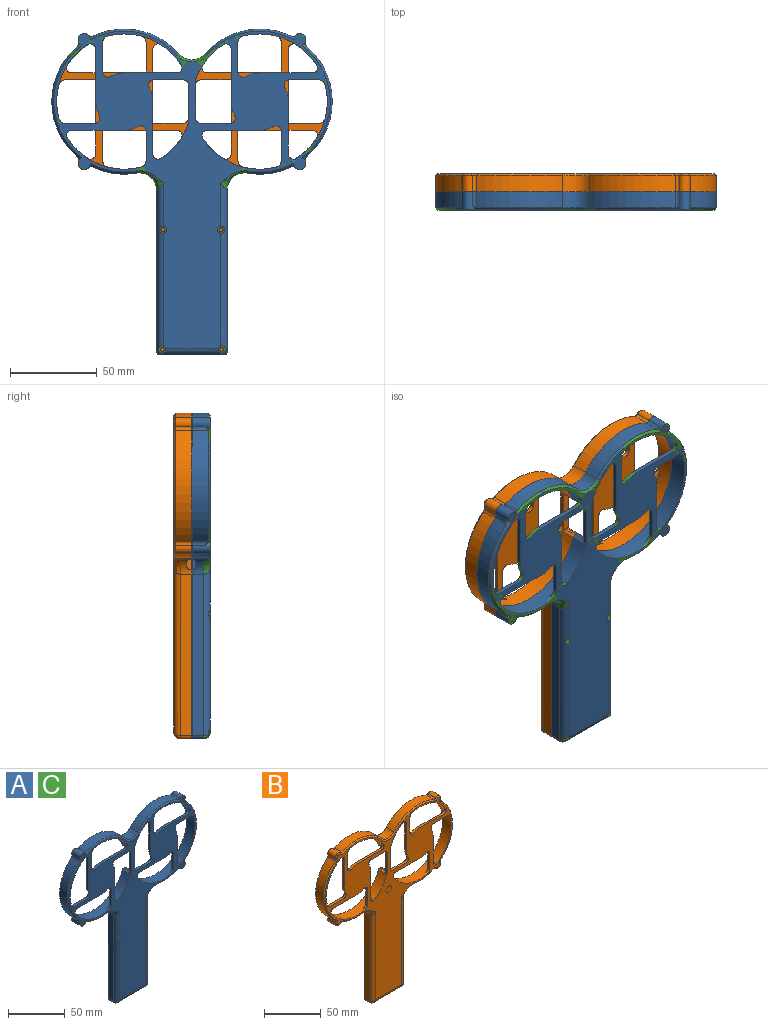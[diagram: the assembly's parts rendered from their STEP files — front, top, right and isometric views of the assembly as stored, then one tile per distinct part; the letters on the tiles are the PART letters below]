
ASSEMBLY  parts=3 mates=1
PART A: 186 faces, bbox 165x21x189.8 mm
  f0: plane 48.31x37.47mm, normal (0,1,0), area 1443.2mm2, adj f1,f2,f3,f5,f74,f105,f107,f110
  f1: cylinder r=41.8mm len=8.1mm, axis (0,-1,0), area 84.8mm2, adj f0,f4,f105,f185
  f2: plane 32.31x8.1mm, normal (1,0,0), area 230.3mm2, adj f0,f4,f71,f72,f76,f107,f166,f167
  f3: plane 32.31x8.1mm, normal (-1,0,0), area 190.4mm2, adj f0,f4,f110,f163,f164,f165,f185
  f4: plane 187.8x161.6mm, normal (0,1,0), area 2237.1mm2, adj f1,f2,f3,f13,f14,f15,f16,f17
  f5: plane 28.29x8.1mm, normal (0,0,1), area 199.2mm2, adj f0,f23,f107,f110,f155,f158,f159,f161
  f6: plane 28.29x8.1mm, normal (0,0,-1), area 199.2mm2, adj f23,f75,f108,f109,f155,f158,f160,f162
  f7: cylinder r=2.1mm len=4.2mm, axis (0,-1,0), area 31.7mm2, adj f125,f139
  f8: cylinder r=2.1mm len=4.2mm, axis (0,-1,0), area 31.7mm2, adj f126,f138
  f9: cylinder r=2.1mm len=4.2mm, axis (0,-1,0), area 31.7mm2, adj f129,f137
  f10: cylinder r=2.1mm len=4.2mm, axis (0,-1,0), area 31.7mm2, adj f124,f136
  f11: cylinder r=2.1mm len=4.2mm, axis (0,-1,0), area 31.7mm2, adj f127,f135
  f12: cylinder r=2.1mm len=4.2mm, axis (0,-1,0), area 31.7mm2, adj f128,f134
  f13: cylinder r=1.1mm len=7.8mm, axis (0,1,0), area 53.9mm2, adj f4,f116
  f14: cylinder r=1.1mm len=7.8mm, axis (0,1,0), area 53.9mm2, adj f4,f120
  f15: cylinder r=1.1mm len=7.8mm, axis (0,1,0), area 53.9mm2, adj f4,f129
  f16: cylinder r=1.1mm len=7.8mm, axis (0,1,0), area 53.9mm2, adj f4,f128
  f17: cylinder r=1.1mm len=7.8mm, axis (0,1,0), area 53.9mm2, adj f4,f127
  f18: cylinder r=1.1mm len=7.8mm, axis (0,1,0), area 53.9mm2, adj f4,f118
  f19: cylinder r=1.1mm len=7.8mm, axis (0,1,0), area 53.9mm2, adj f4,f122
  f20: cylinder r=1.1mm len=7.8mm, axis (0,1,0), area 53.9mm2, adj f4,f126
  f21: cylinder r=1.1mm len=7.8mm, axis (0,1,0), area 53.9mm2, adj f4,f125
  f22: cylinder r=1.1mm len=7.8mm, axis (0,1,0), area 53.9mm2, adj f4,f124
  f23: plane 24.29x2.8mm, normal (0,1,0), area 67.2mm2, adj f5,f6,f154,f157,f159,f160,f161,f162
  f24: plane 29x8.1mm, normal (0,0,1), area 234.9mm2, adj f4,f75,f111,f112
  f25: plane 63.48x8.1mm, normal (-1,0,0), area 514.2mm2, adj f4,f75,f109,f112
  f26: plane 63.48x8.1mm, normal (1,0,0), area 514.2mm2, adj f4,f75,f108,f111
  f27: cylinder r=41.8mm len=25.51mm, axis (0,1,0), area 241.6mm2, adj f4,f142,f143,f149,f178
  f28: plane 92.94x6.5mm, normal (-1,0,0), area 604.1mm2, adj f4,f115,f132,f142
  f29: plane 36.6x6.5mm, normal (0,0,-1), area 237.9mm2, adj f4,f114,f130,f132
  f30: plane 92.94x6.5mm, normal (1,0,0), area 552.8mm2, adj f4,f113,f130,f140,f163,f164,f165
  f31: cylinder r=41.8mm len=25.51mm, axis (0,1,0), area 241.6mm2, adj f4,f140,f141,f147,f182
  f32: cylinder r=3.5mm len=10.5mm, axis (0,1,0), area 109.8mm2, adj f4,f68,f147,f151,f181,f182
  f33: cylinder r=41.8mm len=63.95mm, axis (0,1,0), area 677.1mm2, adj f4,f151,f180,f181
  f34: cylinder r=3.5mm len=10.5mm, axis (0,1,0), area 109.8mm2, adj f4,f68,f146,f151,f180,f183
  f35: cylinder r=41.8mm len=49.73mm, axis (0,1,0), area 507.1mm2, adj f4,f106,f146,f183
  f36: cylinder r=41.8mm len=49.73mm, axis (0,1,0), area 507.1mm2, adj f4,f106,f144,f179
  f37: cylinder r=3.5mm len=10.5mm, axis (0,1,0), area 109.8mm2, adj f4,f68,f144,f152,f177,f179
  f38: cylinder r=41.8mm len=63.95mm, axis (0,1,0), area 677.1mm2, adj f4,f152,f176,f177
  f39: plane 16.92x2.4mm, normal (-1,0,0), area 40.6mm2, adj f68,f69,f94,f98
  f40: plane 30.26x2.4mm, normal (0,0,-1), area 72.6mm2, adj f59,f68,f69,f93
  f41: plane 30.26x2.4mm, normal (-1,0,0), area 72.6mm2, adj f42,f68,f69,f91
  f42: cylinder r=16.5mm len=8.04mm, axis (0,1,0), area 20.2mm2, adj f41,f68,f69,f92
  f43: plane 30.26x2.4mm, normal (0,0,1), area 72.6mm2, adj f44,f68,f69,f89
  f44: cylinder r=16.5mm len=8.04mm, axis (0,1,0), area 20.2mm2, adj f43,f68,f69,f90
  f45: cylinder r=39mm len=78mm, axis (0,1,0), area 2168.6mm2, adj f4,f62,f68,f69,f86,f89,f91,f93
  f46: plane 30.26x2.4mm, normal (1,0,0), area 72.6mm2, adj f47,f68,f69,f86
  f47: cylinder r=16.5mm len=8.04mm, axis (0,1,0), area 20.2mm2, adj f46,f68,f69,f87
  f48: plane 16.91x2.4mm, normal (0,0,-1), area 40.6mm2, adj f68,f69,f87,f88
  f49: plane 16.92x2.4mm, normal (-1,0,0), area 40.6mm2, adj f68,f69,f85,f95
  f50: cylinder r=39mm len=78mm, axis (0,1,0), area 2168.6mm2, adj f4,f64,f68,f69,f77,f79,f81,f84
  f51: plane 30.26x2.4mm, normal (0,0,-1), area 72.6mm2, adj f63,f68,f69,f84
  f52: plane 30.26x2.4mm, normal (-1,0,0), area 72.6mm2, adj f53,f68,f69,f81
  f53: cylinder r=16.5mm len=8.04mm, axis (0,1,0), area 20.2mm2, adj f52,f68,f69,f82
  f54: plane 16.91x2.4mm, normal (0,0,1), area 40.6mm2, adj f68,f69,f82,f83
  f55: plane 30.26x2.4mm, normal (0,0,1), area 72.6mm2, adj f56,f68,f69,f79
  f56: cylinder r=16.5mm len=8.04mm, axis (0,1,0), area 20.2mm2, adj f55,f68,f69,f80
  f57: plane 30.26x2.4mm, normal (1,0,0), area 72.6mm2, adj f58,f68,f69,f77
  f58: cylinder r=16.5mm len=8.04mm, axis (0,1,0), area 20.2mm2, adj f57,f68,f69,f78
  f59: cylinder r=16.5mm len=8.04mm, axis (0,1,0), area 20.2mm2, adj f40,f68,f69,f94
  f60: plane 16.92x2.4mm, normal (0,0,1), area 40.6mm2, adj f68,f69,f92,f100
  f61: plane 16.92x2.4mm, normal (1,0,0), area 40.6mm2, adj f68,f69,f90,f99
  f62: plane 22x2.4mm, normal (-1,0,0), area 52.8mm2, adj f45,f68,f69,f88
  f63: cylinder r=16.5mm len=8.04mm, axis (0,1,0), area 20.2mm2, adj f51,f68,f69,f85
  f64: plane 22x2.4mm, normal (1,0,0), area 52.8mm2, adj f50,f68,f69,f83
  f65: plane 16.92x2.4mm, normal (1,0,0), area 40.6mm2, adj f68,f69,f80,f97
  f66: plane 16.92x2.4mm, normal (0,0,-1), area 40.6mm2, adj f68,f69,f78,f96
  f67: cylinder r=3.5mm len=10.5mm, axis (0,1,0), area 109.8mm2, adj f4,f68,f149,f152,f176,f178
  f68: plane 183.14x159.74mm, normal (0,-1,0), area 7702.7mm2, adj f32,f34,f37,f39,f40,f41,f42,f43
  f69: plane 153.67x75.67mm, normal (0,1,0), area 2861.2mm2, adj f39,f40,f41,f42,f43,f44,f45,f46
  f70: plane 8.1x1.3mm, normal (0,0,-1), area 10.5mm2, adj f4,f69,f101,f102
  f71: plane 3.16x0.8mm, normal (0,0,1), area 2.5mm2, adj f2,f4,f142,f167
  f72: plane 7.81x0.8mm, normal (0,0,-1), area 6.2mm2, adj f2,f4,f142,f166
  f73: plane 8.1x1.3mm, normal (0,0,1), area 10.5mm2, adj f4,f69,f103,f104
  f74: cylinder r=41.8mm len=8.1mm, axis (0,-1,0), area 84.8mm2, adj f0,f4,f105,f184
  f75: plane 68x35mm, normal (0,1,0), area 2357.6mm2, adj f6,f24,f25,f26,f108,f109,f111,f112
  f76: plane 6.38x4mm, normal (0,1,0), area 18.7mm2, adj f2,f142,f166,f167
  f77: cylinder r=3mm len=4.63mm, axis (0,1,0), area 15.4mm2, adj f50,f57,f68,f69
  f78: cylinder r=3mm len=4.46mm, axis (0,1,0), area 15mm2, adj f58,f66,f68,f69
  f79: cylinder r=3mm len=4.63mm, axis (0,1,0), area 15.4mm2, adj f50,f55,f68,f69
  f80: cylinder r=3mm len=4.46mm, axis (0,1,0), area 15mm2, adj f56,f65,f68,f69
  f81: cylinder r=3mm len=4.63mm, axis (0,1,0), area 15.4mm2, adj f50,f52,f68,f69
  f82: cylinder r=3mm len=4.46mm, axis (0,1,0), area 15mm2, adj f53,f54,f68,f69
  f83: cylinder r=3mm len=3mm, axis (0,1,0), area 11.3mm2, adj f54,f64,f68,f69
  f84: cylinder r=3mm len=4.63mm, axis (0,1,0), area 15.4mm2, adj f50,f51,f68,f69
  f85: cylinder r=3mm len=4.46mm, axis (0,1,0), area 15mm2, adj f49,f63,f68,f69
  f86: cylinder r=3mm len=4.63mm, axis (0,1,0), area 15.4mm2, adj f45,f46,f68,f69
  f87: cylinder r=3mm len=4.46mm, axis (0,1,0), area 15mm2, adj f47,f48,f68,f69
  f88: cylinder r=3mm len=3mm, axis (0,-1,0), area 11.3mm2, adj f48,f62,f68,f69
  f89: cylinder r=3mm len=4.63mm, axis (0,1,0), area 15.4mm2, adj f43,f45,f68,f69
  f90: cylinder r=3mm len=4.46mm, axis (0,1,0), area 15mm2, adj f44,f61,f68,f69
  f91: cylinder r=3mm len=4.63mm, axis (0,1,0), area 15.4mm2, adj f41,f45,f68,f69
  f92: cylinder r=3mm len=4.46mm, axis (0,1,0), area 15mm2, adj f42,f60,f68,f69
  f93: cylinder r=3mm len=4.63mm, axis (0,1,0), area 15.4mm2, adj f40,f45,f68,f69
  f94: cylinder r=3mm len=4.46mm, axis (0,1,0), area 15mm2, adj f39,f59,f68,f69
  f95: cylinder r=4mm len=3.88mm, axis (0,1,0), area 12.7mm2, adj f49,f50,f68,f69
  f96: cylinder r=4mm len=3.88mm, axis (0,1,0), area 12.7mm2, adj f50,f66,f68,f69
  f97: cylinder r=4mm len=3.88mm, axis (0,1,0), area 12.7mm2, adj f50,f65,f68,f69
  f98: cylinder r=4mm len=3.88mm, axis (0,1,0), area 12.7mm2, adj f39,f45,f68,f69
  f99: cylinder r=4mm len=3.88mm, axis (0,1,0), area 12.7mm2, adj f45,f61,f68,f69
  f100: cylinder r=4mm len=3.88mm, axis (0,1,0), area 12.7mm2, adj f45,f60,f68,f69
  f101: cylinder r=2mm len=8.1mm, axis (0,1,0), area 19.6mm2, adj f4,f45,f69,f70
  f102: cylinder r=2mm len=8.1mm, axis (0,1,0), area 19.6mm2, adj f4,f50,f69,f70
  f103: cylinder r=2mm len=8.1mm, axis (0,1,0), area 19.6mm2, adj f4,f50,f69,f73
  f104: cylinder r=2mm len=8.1mm, axis (0,1,0), area 19.6mm2, adj f4,f45,f69,f73
  f105: cylinder r=10mm len=15.06mm, axis (0,1,0), area 138.1mm2, adj f0,f1,f4,f74
  f106: cylinder r=10mm len=15.06mm, axis (0,-1,0), area 158.6mm2, adj f4,f35,f36,f145
  f107: cylinder r=3mm len=8.1mm, axis (0,1,0), area 32.1mm2, adj f0,f2,f4,f5,f153
  f108: cylinder r=3mm len=8.1mm, axis (0,1,0), area 32.1mm2, adj f4,f6,f26,f75,f153
  f109: cylinder r=3mm len=8.1mm, axis (0,1,0), area 32.1mm2, adj f4,f6,f25,f75,f156
  f110: cylinder r=3mm len=8.1mm, axis (0,1,0), area 32.1mm2, adj f0,f3,f4,f5,f156
  f111: cylinder r=3mm len=8.1mm, axis (0,1,0), area 38.2mm2, adj f4,f24,f26,f75
  f112: cylinder r=3mm len=8.1mm, axis (0,1,0), area 38.2mm2, adj f4,f24,f25,f75
  f113: cylinder r=4mm len=97.44mm, axis (0,0,-1), area 551.9mm2, adj f0,f30,f68,f121,f123,f131,f141,f163
  f114: cylinder r=4mm len=36.6mm, axis (-1,0,0), area 209.4mm2, adj f29,f68,f117,f121,f131,f133
  f115: cylinder r=4mm len=97.44mm, axis (0,0,1), area 572.4mm2, adj f28,f68,f117,f119,f133,f143
  f116: plane 4.2x4.2mm, normal (0,-1,0), area 10.1mm2, adj f13,f117
  f117: cylinder r=2.1mm len=4.2mm, axis (0,-1,0), area 27mm2, adj f68,f114,f115,f116,f133
  f118: plane 4.2x4.2mm, normal (0,-1,0), area 10.1mm2, adj f18,f119
  f119: cylinder r=2.1mm len=4.2mm, axis (0,-1,0), area 32.2mm2, adj f68,f115,f118
  f120: plane 4.2x4.2mm, normal (0,-1,0), area 10.1mm2, adj f14,f121
  f121: cylinder r=2.1mm len=4.2mm, axis (0,-1,0), area 27mm2, adj f68,f113,f114,f120,f131
  f122: plane 4.2x4.2mm, normal (0,-1,0), area 10.1mm2, adj f19,f123
  f123: cylinder r=2.1mm len=4.2mm, axis (0,-1,0), area 32.2mm2, adj f68,f113,f122
  f124: plane 4.2x4.2mm, normal (0,-1,0), area 10.1mm2, adj f10,f22
  f125: plane 4.2x4.2mm, normal (0,-1,0), area 10.1mm2, adj f7,f21
  f126: plane 4.2x4.2mm, normal (0,-1,0), area 10.1mm2, adj f8,f20
  f127: plane 4.2x4.2mm, normal (0,-1,0), area 10.1mm2, adj f11,f17
  f128: plane 4.2x4.2mm, normal (0,-1,0), area 10.1mm2, adj f12,f16
  f129: plane 4.2x4.2mm, normal (0,-1,0), area 10.1mm2, adj f9,f15
  f130: cylinder r=2mm len=6.5mm, axis (0,-1,0), area 20.4mm2, adj f4,f29,f30,f131
  f131: bspline ~4.15x2.63mm, area 9.6mm2, adj f113,f114,f121,f130
  f132: cylinder r=2mm len=6.5mm, axis (0,1,0), area 20.4mm2, adj f4,f28,f29,f133
  f133: bspline ~4.15x2.63mm, area 9.6mm2, adj f114,f115,f117,f132
  f134: plane 4.2x4.2mm, normal (0,1,0), area 13.9mm2, adj f12
  f135: plane 4.2x4.2mm, normal (0,1,0), area 13.9mm2, adj f11
  f136: plane 4.2x4.2mm, normal (0,1,0), area 13.9mm2, adj f10
  f137: plane 4.2x4.2mm, normal (0,1,0), area 13.9mm2, adj f9
  f138: plane 4.2x4.2mm, normal (0,1,0), area 13.9mm2, adj f8
  f139: plane 4.2x4.2mm, normal (0,1,0), area 13.9mm2, adj f7
  f140: cylinder r=10mm len=11.68mm, axis (0,1,0), area 113.1mm2, adj f4,f30,f31,f141
  f141: bspline ~15.99x15.59mm, area 67.2mm2, adj f31,f113,f140,f148
  f142: cylinder r=10mm len=11.68mm, axis (0,1,0), area 100.5mm2, adj f4,f27,f28,f71,f72,f76,f143,f166
  f143: bspline ~15.99x15.59mm, area 67.2mm2, adj f27,f115,f142,f150
  f144: cone r=40.6mm half-angle=45deg, axis (0,1,0), area 96.2mm2, adj f36,f37,f68,f145,f179
  f145: cone r=11.2mm half-angle=45deg, axis (0,-1,0), area 30.7mm2, adj f68,f106,f144,f146
  f146: cone r=40.6mm half-angle=45deg, axis (0,1,0), area 96.2mm2, adj f34,f35,f68,f145,f183
  f147: cone r=40.6mm half-angle=45deg, axis (0,1,0), area 48.8mm2, adj f31,f32,f68,f148,f182
  f148: bspline ~15.66x6.83mm, area 12.3mm2, adj f68,f141,f147
  f149: cone r=40.6mm half-angle=45deg, axis (0,1,0), area 48.8mm2, adj f27,f67,f68,f150,f178
  f150: bspline ~15.66x6.83mm, area 12.3mm2, adj f68,f143,f149
  f151: cone r=40.6mm half-angle=45deg, axis (0,1,0), area 131.8mm2, adj f32,f33,f34,f68,f180,f181
  f152: cone r=40.6mm half-angle=45deg, axis (0,1,0), area 131.8mm2, adj f37,f38,f67,f68,f176,f177
  f153: plane 5x2.8mm, normal (1,0,0), area 14mm2, adj f4,f107,f108,f155
  f154: plane 5x0.8mm, normal (-1,0,0), area 4mm2, adj f23,f155,f159,f160
  f155: plane 3x2.8mm, normal (0,1,0), area 6mm2, adj f5,f6,f153,f154,f159,f160
  f156: plane 5x2.8mm, normal (-1,0,0), area 14mm2, adj f4,f109,f110,f158
  f157: plane 5x0.8mm, normal (1,0,0), area 4mm2, adj f23,f158,f161,f162
  f158: plane 3x2.8mm, normal (0,1,0), area 6mm2, adj f5,f6,f156,f157,f161,f162
  f159: cylinder r=1mm len=5mm, axis (0,-1,0), area 7.9mm2, adj f5,f23,f154,f155
  f160: cylinder r=1mm len=5mm, axis (0,-1,0), area 7.9mm2, adj f6,f23,f154,f155
  f161: cylinder r=1mm len=5mm, axis (0,1,0), area 7.9mm2, adj f5,f23,f157,f158
  f162: cylinder r=1mm len=5mm, axis (0,1,0), area 7.9mm2, adj f6,f23,f157,f158
  f163: plane 5.7x2.8mm, normal (0,0,-1), area 15.8mm2, adj f0,f3,f30,f113,f164
  f164: plane 12.5x2.8mm, normal (0,-1,0), area 35mm2, adj f3,f30,f163,f165
  f165: plane 5.7x2.8mm, normal (0,0,1), area 15.8mm2, adj f0,f3,f30,f113,f164
  f166: cylinder r=1mm len=7.81mm, axis (1,0,0), area 11.1mm2, adj f2,f72,f76,f142
  f167: cylinder r=1mm len=3.5mm, axis (-1,0,0), area 5.2mm2, adj f2,f71,f76,f142
  f168: plane 5.2x1.5mm, normal (0,0,1), area 7.8mm2, adj f0,f171,f172,f175
  f169: plane 6x1.5mm, normal (1,0,0), area 9mm2, adj f0,f171,f172,f173
  f170: plane 5.2x1.5mm, normal (0,0,-1), area 7.8mm2, adj f0,f171,f173,f174
  f171: plane 14x9.2mm, normal (0,1,0), area 92mm2, adj f2,f168,f169,f170,f172,f173,f174,f175
  f172: cylinder r=2mm len=2mm, axis (0,1,0), area 4.7mm2, adj f0,f168,f169,f171
  f173: cylinder r=2mm len=2mm, axis (0,-1,0), area 4.7mm2, adj f0,f169,f170,f171
  f174: cylinder r=2mm len=2mm, axis (0,1,0), area 4.7mm2, adj f0,f2,f170,f171
  f175: cylinder r=2mm len=2mm, axis (0,-1,0), area 4.7mm2, adj f0,f2,f168,f171
  f176: cylinder r=2mm len=9.3mm, axis (0,-1,0), area 21.8mm2, adj f4,f38,f67,f152
  f177: cylinder r=2mm len=9.3mm, axis (0,-1,0), area 21.8mm2, adj f4,f37,f38,f152
  f178: cylinder r=2mm len=9.3mm, axis (0,-1,0), area 21.8mm2, adj f4,f27,f67,f149
  f179: cylinder r=2mm len=9.3mm, axis (0,-1,0), area 21.8mm2, adj f4,f36,f37,f144
  f180: cylinder r=2mm len=9.3mm, axis (0,-1,0), area 21.8mm2, adj f4,f33,f34,f151
  f181: cylinder r=2mm len=9.3mm, axis (0,-1,0), area 21.8mm2, adj f4,f32,f33,f151
  f182: cylinder r=2mm len=9.3mm, axis (0,-1,0), area 21.8mm2, adj f4,f31,f32,f147
  f183: cylinder r=2mm len=9.3mm, axis (0,-1,0), area 21.8mm2, adj f4,f34,f35,f146
  f184: cylinder r=5mm len=8.1mm, axis (0,-1,0), area 39.2mm2, adj f0,f2,f4,f74
  f185: cylinder r=5mm len=8.1mm, axis (0,-1,0), area 39.2mm2, adj f0,f1,f3,f4
PART B: 181 faces, bbox 162.1x21x188.3 mm
  f0: plane 43.01x35mm, normal (0,1,0), area 1044.3mm2, adj f1,f2,f4,f5,f56,f92,f94,f128
  f1: cylinder r=41.8mm len=8.1mm, axis (0,-1,0), area 57.5mm2, adj f0,f57,f145,f159
  f2: plane 31.8x8.1mm, normal (1,0,0), area 181.9mm2, adj f0,f57,f94,f131,f146,f149,f158
  f3: plane 27x8.1mm, normal (0,0,1), area 218.7mm2, adj f57,f58,f90,f93
  f4: plane 27.18x8.1mm, normal (0,0,1), area 220.2mm2, adj f0,f57,f92,f94
  f5: plane 31.8x8.1mm, normal (-1,0,0), area 240.7mm2, adj f0,f53,f54,f57,f59,f92,f126,f127
  f6: plane 27.18x8.1mm, normal (0,0,-1), area 220.2mm2, adj f57,f58,f89,f91
  f7: plane 61.97x8.1mm, normal (1,0,0), area 502mm2, adj f57,f58,f91,f93
  f8: plane 61.97x8.1mm, normal (-1,0,0), area 502mm2, adj f57,f58,f89,f90
  f9: cylinder r=41.8mm len=25.51mm, axis (0,1,0), area 241.6mm2, adj f57,f124,f125,f157,f179
  f10: plane 92.94x6.5mm, normal (-1,0,0), area 604.1mm2, adj f57,f117,f120,f124
  f11: plane 36.6x6.5mm, normal (0,0,-1), area 237.9mm2, adj f57,f116,f118,f120
  f12: plane 92.94x6.5mm, normal (1,0,0), area 604.1mm2, adj f57,f115,f118,f122
  f13: cylinder r=41.8mm len=25.51mm, axis (0,1,0), area 241.6mm2, adj f57,f122,f123,f156,f161
  f14: cylinder r=3.5mm len=9.3mm, axis (0,1,0), area 90.8mm2, adj f57,f155,f156,f163
  f15: cylinder r=41.8mm len=63.95mm, axis (0,1,0), area 677.1mm2, adj f57,f154,f155,f165
  f16: cylinder r=3.5mm len=9.3mm, axis (0,1,0), area 90.8mm2, adj f57,f152,f154,f167
  f17: cylinder r=41.8mm len=49.73mm, axis (0,1,0), area 507.1mm2, adj f57,f88,f152,f169
  f18: cylinder r=41.8mm len=49.73mm, axis (0,1,0), area 507.1mm2, adj f57,f88,f153,f171
  f19: cylinder r=3.5mm len=9.3mm, axis (0,1,0), area 90.8mm2, adj f57,f150,f153,f173
  f20: cylinder r=41.8mm len=63.95mm, axis (0,1,0), area 677.1mm2, adj f57,f150,f151,f175
  f21: plane 16.92x2.4mm, normal (-1,0,0), area 40.6mm2, adj f50,f51,f77,f81
  f22: plane 30.26x2.4mm, normal (0,0,-1), area 72.6mm2, adj f41,f50,f51,f76
  f23: plane 30.26x2.4mm, normal (-1,0,0), area 72.6mm2, adj f24,f50,f51,f74
  f24: cylinder r=16.5mm len=8.04mm, axis (0,1,0), area 20.2mm2, adj f23,f50,f51,f75
  f25: plane 30.26x2.4mm, normal (0,0,1), area 72.6mm2, adj f26,f50,f51,f72
  f26: cylinder r=16.5mm len=8.04mm, axis (0,1,0), area 20.2mm2, adj f25,f50,f51,f73
  f27: cylinder r=39mm len=78mm, axis (0,1,0), area 2168.6mm2, adj f44,f50,f51,f57,f69,f72,f74,f76
  f28: plane 30.26x2.4mm, normal (1,0,0), area 72.6mm2, adj f29,f50,f51,f69
  f29: cylinder r=16.5mm len=8.04mm, axis (0,1,0), area 20.2mm2, adj f28,f50,f51,f70
  f30: plane 16.91x2.4mm, normal (0,0,-1), area 40.6mm2, adj f50,f51,f70,f71
  f31: plane 16.92x2.4mm, normal (-1,0,0), area 40.6mm2, adj f50,f51,f68,f78
  f32: cylinder r=39mm len=78mm, axis (0,1,0), area 2168.6mm2, adj f46,f50,f51,f57,f60,f62,f64,f67
  f33: plane 30.26x2.4mm, normal (0,0,-1), area 72.6mm2, adj f45,f50,f51,f67
  f34: plane 30.26x2.4mm, normal (-1,0,0), area 72.6mm2, adj f35,f50,f51,f64
  f35: cylinder r=16.5mm len=8.04mm, axis (0,1,0), area 20.2mm2, adj f34,f50,f51,f65
  f36: plane 16.91x2.4mm, normal (0,0,1), area 40.6mm2, adj f50,f51,f65,f66
  f37: plane 30.26x2.4mm, normal (0,0,1), area 72.6mm2, adj f38,f50,f51,f62
  f38: cylinder r=16.5mm len=8.04mm, axis (0,1,0), area 20.2mm2, adj f37,f50,f51,f63
  f39: plane 30.26x2.4mm, normal (1,0,0), area 72.6mm2, adj f40,f50,f51,f60
  f40: cylinder r=16.5mm len=8.04mm, axis (0,1,0), area 20.2mm2, adj f39,f50,f51,f61
  f41: cylinder r=16.5mm len=8.04mm, axis (0,1,0), area 20.2mm2, adj f22,f50,f51,f77
  f42: plane 16.92x2.4mm, normal (0,0,1), area 40.6mm2, adj f50,f51,f75,f83
  f43: plane 16.92x2.4mm, normal (1,0,0), area 40.6mm2, adj f50,f51,f73,f82
  f44: plane 22x2.4mm, normal (-1,0,0), area 52.8mm2, adj f27,f50,f51,f71
  f45: cylinder r=16.5mm len=8.04mm, axis (0,1,0), area 20.2mm2, adj f33,f50,f51,f68
  f46: plane 22x2.4mm, normal (1,0,0), area 52.8mm2, adj f32,f50,f51,f66
  f47: plane 16.92x2.4mm, normal (1,0,0), area 40.6mm2, adj f50,f51,f63,f80
  f48: plane 16.92x2.4mm, normal (0,0,-1), area 40.6mm2, adj f50,f51,f61,f79
  f49: cylinder r=3.5mm len=9.3mm, axis (0,1,0), area 90.8mm2, adj f57,f151,f157,f177
  f50: plane 183.14x159.74mm, normal (0,-1,0), area 7666.5mm2, adj f21,f22,f23,f24,f25,f26,f27,f28
  f51: plane 153.67x75.67mm, normal (0,1,0), area 2861.2mm2, adj f21,f22,f23,f24,f25,f26,f27,f28
  f52: plane 8.1x1.3mm, normal (0,0,-1), area 10.5mm2, adj f51,f57,f84,f85
  f53: plane 7.81x1.1mm, normal (0,0,-1), area 8.6mm2, adj f5,f57,f122,f126
  f54: plane 3.16x1.1mm, normal (0,0,1), area 3.5mm2, adj f5,f57,f122,f127
  f55: plane 8.1x1.3mm, normal (0,0,1), area 10.5mm2, adj f51,f57,f86,f87
  f56: cylinder r=41.8mm len=8.1mm, axis (0,-1,0), area 57.5mm2, adj f0,f57,f144,f158
  f57: plane 187.8x161.6mm, normal (0,1,0), area 2390.9mm2, adj f1,f2,f3,f4,f5,f6,f7,f8
  f58: plane 68x35mm, normal (0,1,0), area 2342.2mm2, adj f3,f6,f7,f8,f89,f90,f91,f93
  f59: plane 5.34x2mm, normal (0,1,0), area 9.2mm2, adj f5,f122,f126,f127
  f60: cylinder r=3mm len=4.63mm, axis (0,1,0), area 15.4mm2, adj f32,f39,f50,f51
  f61: cylinder r=3mm len=4.46mm, axis (0,1,0), area 15mm2, adj f40,f48,f50,f51
  f62: cylinder r=3mm len=4.63mm, axis (0,1,0), area 15.4mm2, adj f32,f37,f50,f51
  f63: cylinder r=3mm len=4.46mm, axis (0,1,0), area 15mm2, adj f38,f47,f50,f51
  f64: cylinder r=3mm len=4.63mm, axis (0,1,0), area 15.4mm2, adj f32,f34,f50,f51
  f65: cylinder r=3mm len=4.46mm, axis (0,1,0), area 15mm2, adj f35,f36,f50,f51
  f66: cylinder r=3mm len=3mm, axis (0,1,0), area 11.3mm2, adj f36,f46,f50,f51
  f67: cylinder r=3mm len=4.63mm, axis (0,1,0), area 15.4mm2, adj f32,f33,f50,f51
  f68: cylinder r=3mm len=4.46mm, axis (0,1,0), area 15mm2, adj f31,f45,f50,f51
  f69: cylinder r=3mm len=4.63mm, axis (0,1,0), area 15.4mm2, adj f27,f28,f50,f51
  f70: cylinder r=3mm len=4.46mm, axis (0,1,0), area 15mm2, adj f29,f30,f50,f51
  f71: cylinder r=3mm len=3mm, axis (0,-1,0), area 11.3mm2, adj f30,f44,f50,f51
  f72: cylinder r=3mm len=4.63mm, axis (0,1,0), area 15.4mm2, adj f25,f27,f50,f51
  f73: cylinder r=3mm len=4.46mm, axis (0,1,0), area 15mm2, adj f26,f43,f50,f51
  f74: cylinder r=3mm len=4.63mm, axis (0,1,0), area 15.4mm2, adj f23,f27,f50,f51
  f75: cylinder r=3mm len=4.46mm, axis (0,1,0), area 15mm2, adj f24,f42,f50,f51
  f76: cylinder r=3mm len=4.63mm, axis (0,1,0), area 15.4mm2, adj f22,f27,f50,f51
  f77: cylinder r=3mm len=4.46mm, axis (0,1,0), area 15mm2, adj f21,f41,f50,f51
  f78: cylinder r=4mm len=3.88mm, axis (0,1,0), area 12.7mm2, adj f31,f32,f50,f51
  f79: cylinder r=4mm len=3.88mm, axis (0,1,0), area 12.7mm2, adj f32,f48,f50,f51
  f80: cylinder r=4mm len=3.88mm, axis (0,1,0), area 12.7mm2, adj f32,f47,f50,f51
  f81: cylinder r=4mm len=3.88mm, axis (0,1,0), area 12.7mm2, adj f21,f27,f50,f51
  f82: cylinder r=4mm len=3.88mm, axis (0,1,0), area 12.7mm2, adj f27,f43,f50,f51
  f83: cylinder r=4mm len=3.88mm, axis (0,1,0), area 12.7mm2, adj f27,f42,f50,f51
  f84: cylinder r=2mm len=8.1mm, axis (0,1,0), area 19.6mm2, adj f27,f51,f52,f57
  f85: cylinder r=2mm len=8.1mm, axis (0,1,0), area 19.6mm2, adj f32,f51,f52,f57
  f86: cylinder r=2mm len=8.1mm, axis (0,1,0), area 19.6mm2, adj f32,f51,f55,f57
  f87: cylinder r=2mm len=8.1mm, axis (0,1,0), area 19.6mm2, adj f27,f51,f55,f57
  f88: cylinder r=10mm len=15.06mm, axis (0,-1,0), area 158.6mm2, adj f17,f18,f57,f170
  f89: cylinder r=3.5mm len=8.1mm, axis (0,1,0), area 38.6mm2, adj f6,f8,f57,f58
  f90: cylinder r=4mm len=8.1mm, axis (0,1,0), area 50.9mm2, adj f3,f8,f57,f58
  f91: cylinder r=3.5mm len=8.1mm, axis (0,1,0), area 38.6mm2, adj f6,f7,f57,f58
  f92: cylinder r=3.5mm len=8.1mm, axis (0,1,0), area 38.6mm2, adj f0,f4,f5,f57
  f93: cylinder r=4mm len=8.1mm, axis (0,1,0), area 50.9mm2, adj f3,f7,f57,f58
  f94: cylinder r=3.5mm len=8.1mm, axis (0,1,0), area 38.6mm2, adj f0,f2,f4,f57
  f95: cylinder r=1.5mm len=5mm, axis (0,1,0), area 47.1mm2, adj f57,f96
  f96: plane 3x3mm, normal (0,1,0), area 7.1mm2, adj f95
  f97: cylinder r=1.5mm len=5mm, axis (0,1,0), area 47.1mm2, adj f57,f98
  f98: plane 3x3mm, normal (0,1,0), area 7.1mm2, adj f97
  f99: cylinder r=1.5mm len=5mm, axis (0,1,0), area 47.1mm2, adj f57,f100
  f100: plane 3x3mm, normal (0,1,0), area 7.1mm2, adj f99
  f101: cylinder r=1.5mm len=5mm, axis (0,1,0), area 47.1mm2, adj f57,f102
  f102: plane 3x3mm, normal (0,1,0), area 7.1mm2, adj f101
  f103: cylinder r=1.5mm len=5mm, axis (0,1,0), area 47.1mm2, adj f57,f104
  f104: plane 3x3mm, normal (0,1,0), area 7.1mm2, adj f103
  f105: cylinder r=1.5mm len=5mm, axis (0,1,0), area 47.1mm2, adj f57,f106
  f106: plane 3x3mm, normal (0,1,0), area 7.1mm2, adj f105
  f107: cylinder r=1.5mm len=5mm, axis (0,1,0), area 47.1mm2, adj f57,f108
  f108: plane 3x3mm, normal (0,1,0), area 7.1mm2, adj f107
  f109: cylinder r=1.5mm len=5mm, axis (0,1,0), area 47.1mm2, adj f57,f110
  f110: plane 3x3mm, normal (0,1,0), area 7.1mm2, adj f109
  f111: cylinder r=1.5mm len=5mm, axis (0,1,0), area 47.1mm2, adj f57,f112
  f112: plane 3x3mm, normal (0,1,0), area 7.1mm2, adj f111
  f113: cylinder r=1.5mm len=5mm, axis (0,1,0), area 47.1mm2, adj f57,f114
  f114: plane 3x3mm, normal (0,1,0), area 7.1mm2, adj f113
  f115: cylinder r=4mm len=97.44mm, axis (0,0,-1), area 591.8mm2, adj f12,f50,f119,f123
  f116: cylinder r=4mm len=36.6mm, axis (-1,0,0), area 217.4mm2, adj f11,f50,f119,f121
  f117: cylinder r=4mm len=97.44mm, axis (0,0,1), area 591.8mm2, adj f10,f50,f121,f125
  f118: cylinder r=2mm len=6.5mm, axis (0,-1,0), area 20.4mm2, adj f11,f12,f57,f119
  f119: bspline ~4.78x4mm, area 8.7mm2, adj f115,f116,f118
  f120: cylinder r=2mm len=6.5mm, axis (0,1,0), area 20.4mm2, adj f10,f11,f57,f121
  f121: bspline ~4.78x4mm, area 8.7mm2, adj f116,f117,f120
  f122: cylinder r=10mm len=11.68mm, axis (0,1,0), area 91.4mm2, adj f12,f13,f53,f54,f57,f59,f123,f126
  f123: bspline ~15.99x15.59mm, area 67.2mm2, adj f13,f115,f122,f160
  f124: cylinder r=10mm len=11.68mm, axis (0,1,0), area 113.1mm2, adj f9,f10,f57,f125
  f125: bspline ~15.99x15.59mm, area 67.2mm2, adj f9,f117,f124,f180
  f126: cylinder r=2mm len=7.81mm, axis (1,0,0), area 20.7mm2, adj f5,f53,f59,f122
  f127: cylinder r=2mm len=3.95mm, axis (-1,0,0), area 11.2mm2, adj f5,f54,f59,f122
  f128: plane 13x3.6mm, normal (0,0,1), area 46.8mm2, adj f0,f131,f146,f147
  f129: plane 13x3.6mm, normal (1,0,0), area 46.8mm2, adj f0,f131,f147,f148
  f130: plane 13x3.6mm, normal (0,0,-1), area 46.8mm2, adj f0,f131,f148,f149
  f131: plane 21x17mm, normal (0,1,0), area 289mm2, adj f2,f128,f129,f130,f146,f147,f148,f149
  f132: plane 8.1x3.7mm, normal (1,0,0), area 30mm2, adj f0,f57,f142,f145
  f133: plane 8.9x8.1mm, normal (0,0,-1), area 72.1mm2, adj f0,f57,f142,f143
  f134: plane 8.1x3.7mm, normal (-1,0,0), area 30mm2, adj f0,f57,f143,f144
  f135: plane 8.9x8.1mm, normal (-1,0,0), area 72.1mm2, adj f57,f136,f138,f141
  f136: plane 8.9x8.1mm, normal (0,0,-1), area 72.1mm2, adj f57,f135,f137,f141
  f137: plane 8.9x8.1mm, normal (1,0,0), area 72.1mm2, adj f57,f136,f138,f141
  f138: plane 8.9x8.1mm, normal (0,0,1), area 72.1mm2, adj f57,f135,f137,f141
  f139: plane 7x7mm, normal (0,1,0), area 38.5mm2, adj f140
  f140: cylinder r=3.5mm len=7mm, axis (0,1,0), area 46.2mm2, adj f139,f141
  f141: plane 8.9x8.9mm, normal (0,1,0), area 40.7mm2, adj f135,f136,f137,f138,f140
  f142: cylinder r=2mm len=8.1mm, axis (0,1,0), area 25.4mm2, adj f0,f57,f132,f133
  f143: cylinder r=2mm len=8.1mm, axis (0,-1,0), area 25.4mm2, adj f0,f57,f133,f134
  f144: cylinder r=2mm len=8.1mm, axis (0,-1,0), area 38mm2, adj f0,f56,f57,f134
  f145: cylinder r=2mm len=8.1mm, axis (0,-1,0), area 38mm2, adj f0,f1,f57,f132
  f146: cylinder r=2mm len=3.6mm, axis (0,1,0), area 11.3mm2, adj f0,f2,f128,f131
  f147: cylinder r=2mm len=3.6mm, axis (0,-1,0), area 11.3mm2, adj f0,f128,f129,f131
  f148: cylinder r=2mm len=3.6mm, axis (0,1,0), area 11.3mm2, adj f0,f129,f130,f131
  f149: cylinder r=2mm len=3.6mm, axis (0,-1,0), area 11.3mm2, adj f0,f2,f130,f131
  f150: cylinder r=2mm len=9.3mm, axis (0,-1,0), area 23.6mm2, adj f19,f20,f57,f174
  f151: cylinder r=2mm len=9.3mm, axis (0,-1,0), area 23.6mm2, adj f20,f49,f57,f176
  f152: cylinder r=2mm len=9.3mm, axis (0,-1,0), area 23.6mm2, adj f16,f17,f57,f168
  f153: cylinder r=2mm len=9.3mm, axis (0,-1,0), area 23.6mm2, adj f18,f19,f57,f172
  f154: cylinder r=2mm len=9.3mm, axis (0,-1,0), area 23.6mm2, adj f15,f16,f57,f166
  f155: cylinder r=2mm len=9.3mm, axis (0,-1,0), area 23.6mm2, adj f14,f15,f57,f164
  f156: cylinder r=2mm len=9.3mm, axis (0,-1,0), area 23.6mm2, adj f13,f14,f57,f162
  f157: cylinder r=2mm len=9.3mm, axis (0,-1,0), area 23.6mm2, adj f9,f49,f57,f178
  f158: cylinder r=5mm len=8.1mm, axis (0,-1,0), area 39.2mm2, adj f0,f2,f56,f57
  f159: cylinder r=5mm len=8.1mm, axis (0,-1,0), area 39.2mm2, adj f0,f1,f5,f57
  f160: bspline ~15.66x6.83mm, area 12.3mm2, adj f50,f123,f161
  f161: cone r=40.6mm half-angle=45deg, axis (0,1,0), area 43.8mm2, adj f13,f50,f160,f162
  f162: cone r=3.2mm half-angle=45deg, axis (0,-1,0), area 5.6mm2, adj f50,f156,f161,f163
  f163: cone r=2.3mm half-angle=45deg, axis (0,1,0), area 13.7mm2, adj f14,f50,f162,f164
  f164: cone r=3.2mm half-angle=45deg, axis (0,-1,0), area 5.6mm2, adj f50,f155,f163,f165
  f165: cone r=40.6mm half-angle=45deg, axis (0,1,0), area 121.8mm2, adj f15,f50,f164,f166
  f166: cone r=3.2mm half-angle=45deg, axis (0,-1,0), area 5.6mm2, adj f50,f154,f165,f167
  f167: cone r=2.3mm half-angle=45deg, axis (0,1,0), area 13.7mm2, adj f16,f50,f166,f168
  f168: cone r=3.2mm half-angle=45deg, axis (0,-1,0), area 5.6mm2, adj f50,f152,f167,f169
  f169: cone r=40.6mm half-angle=45deg, axis (0,1,0), area 91.2mm2, adj f17,f50,f168,f170
  f170: cone r=11.2mm half-angle=45deg, axis (0,-1,0), area 30.7mm2, adj f50,f88,f169,f171
  f171: cone r=40.6mm half-angle=45deg, axis (0,1,0), area 91.2mm2, adj f18,f50,f170,f172
  f172: cone r=3.2mm half-angle=45deg, axis (0,-1,0), area 5.6mm2, adj f50,f153,f171,f173
  f173: cone r=2.3mm half-angle=45deg, axis (0,1,0), area 13.7mm2, adj f19,f50,f172,f174
  f174: cone r=3.2mm half-angle=45deg, axis (0,-1,0), area 5.6mm2, adj f50,f150,f173,f175
  f175: cone r=40.6mm half-angle=45deg, axis (0,1,0), area 121.8mm2, adj f20,f50,f174,f176
  f176: cone r=3.2mm half-angle=45deg, axis (0,-1,0), area 5.6mm2, adj f50,f151,f175,f177
  f177: cone r=2.3mm half-angle=45deg, axis (0,1,0), area 13.7mm2, adj f49,f50,f176,f178
  f178: cone r=3.2mm half-angle=45deg, axis (0,-1,0), area 5.6mm2, adj f50,f157,f177,f179
  f179: cone r=40.6mm half-angle=45deg, axis (0,1,0), area 43.8mm2, adj f9,f50,f178,f180
  f180: bspline ~15.66x6.83mm, area 12.3mm2, adj f50,f125,f179
PART C: same geometry as A
PLACE A t=(10.43,0.28,0.68)mm
PLACE B rot(axis=(0,0,1),180deg) t=(10.43,16.48,0.68)mm
PLACE C t=(10.43,0.28,0.68)mm
MATE fastened B.f91 <-> A.f19  axis (0,-1,0) through (27.23,8.38,-73.12)mm
